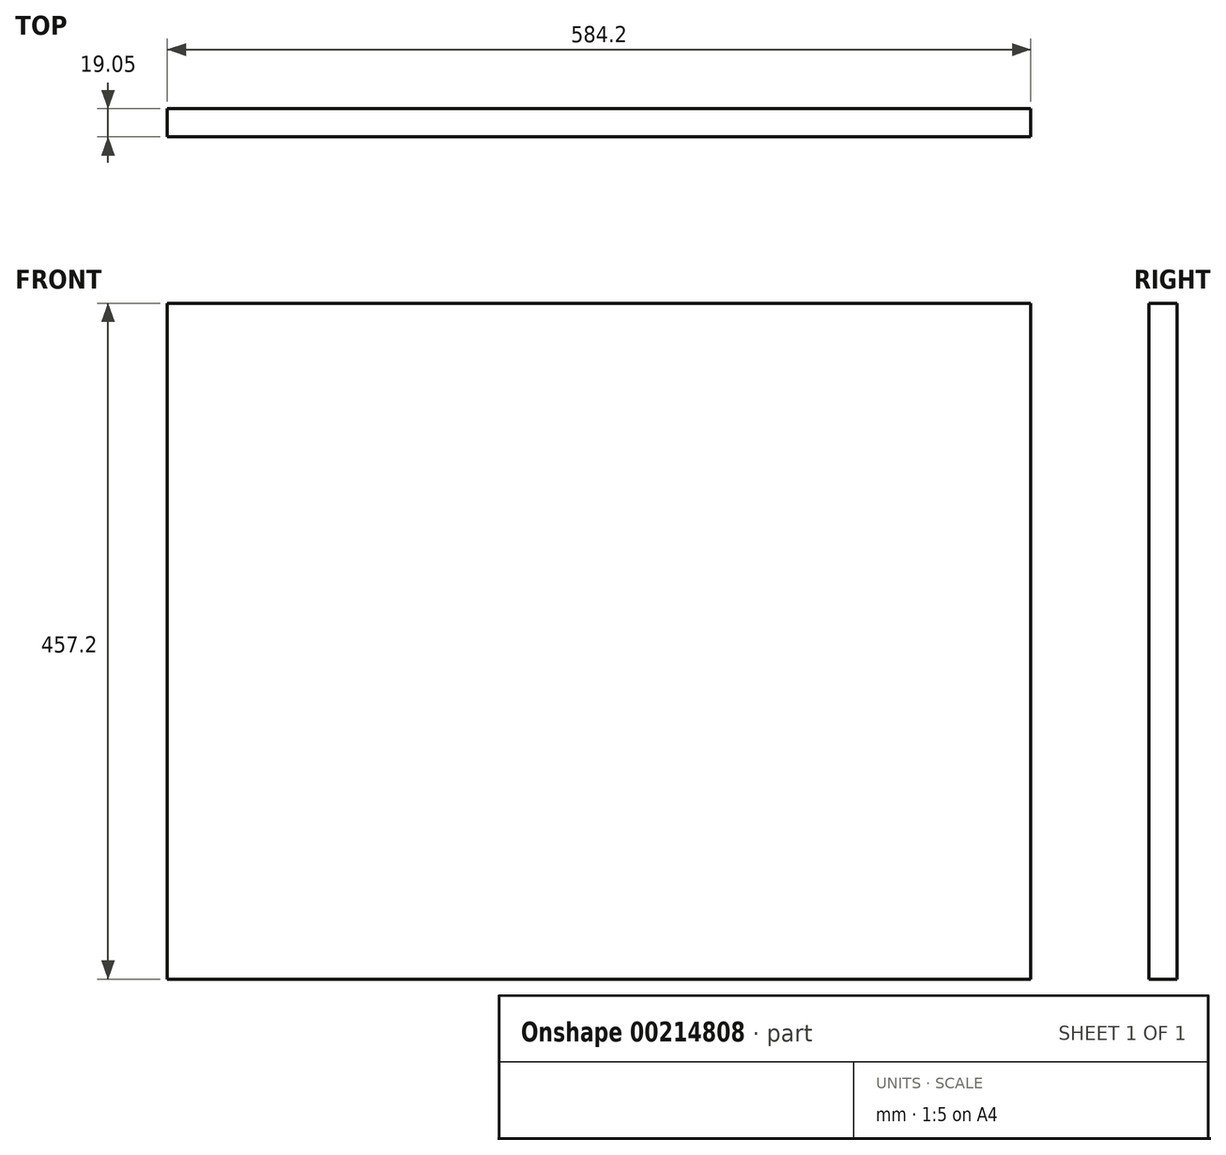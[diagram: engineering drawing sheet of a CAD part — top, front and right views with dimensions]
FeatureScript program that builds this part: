
annotation { "Feature Type Name" : "Feature", "Feature Type Description" : "" }
export const myFeature = defineFeature(function(context is Context, id is Id, definition is map)
    precondition{}
    {
        {
            var Q0;
            Q0=qCreatedBy(makeId("Front.planeOp"),FACE);
            var sketch = newSketch(context, id + "F0", { "sketchPlane" : qUnion([Q0])});
            skLineSegment(sketch, "E0.bottom", {"start": v(0, 0) * mm, "end": v(584.2, 0) * mm});
            skLineSegment(sketch, "E0.top", {"start": v(0, -457.2) * mm, "end": v(584.2, -457.2) * mm});
            skLineSegment(sketch, "E0.left", {"start": v(0, 0) * mm, "end": v(0, -457.2) * mm});
            skLineSegment(sketch, "E0.right", {"start": v(584.2, 0) * mm, "end": v(584.2, -457.2) * mm});
            skSolve(sketch);
        }
        {
            var Q0;
            Q0=makeQuery(id+"F0.imprint","IMPRINT",FACE,{"disambiguationData":[TD([[makeQuery(id+"F0.imprint","IMPRINT",EDGE,{"derivedFrom":sQuery(id+"F0.wireOp",EDGE,"E0.bottom")}),-1.0]])]});
            extrude(context, id + "F1", {"entities" : qUnion([Q0]), "depth" : 19.05 * mm});
        }
    });
